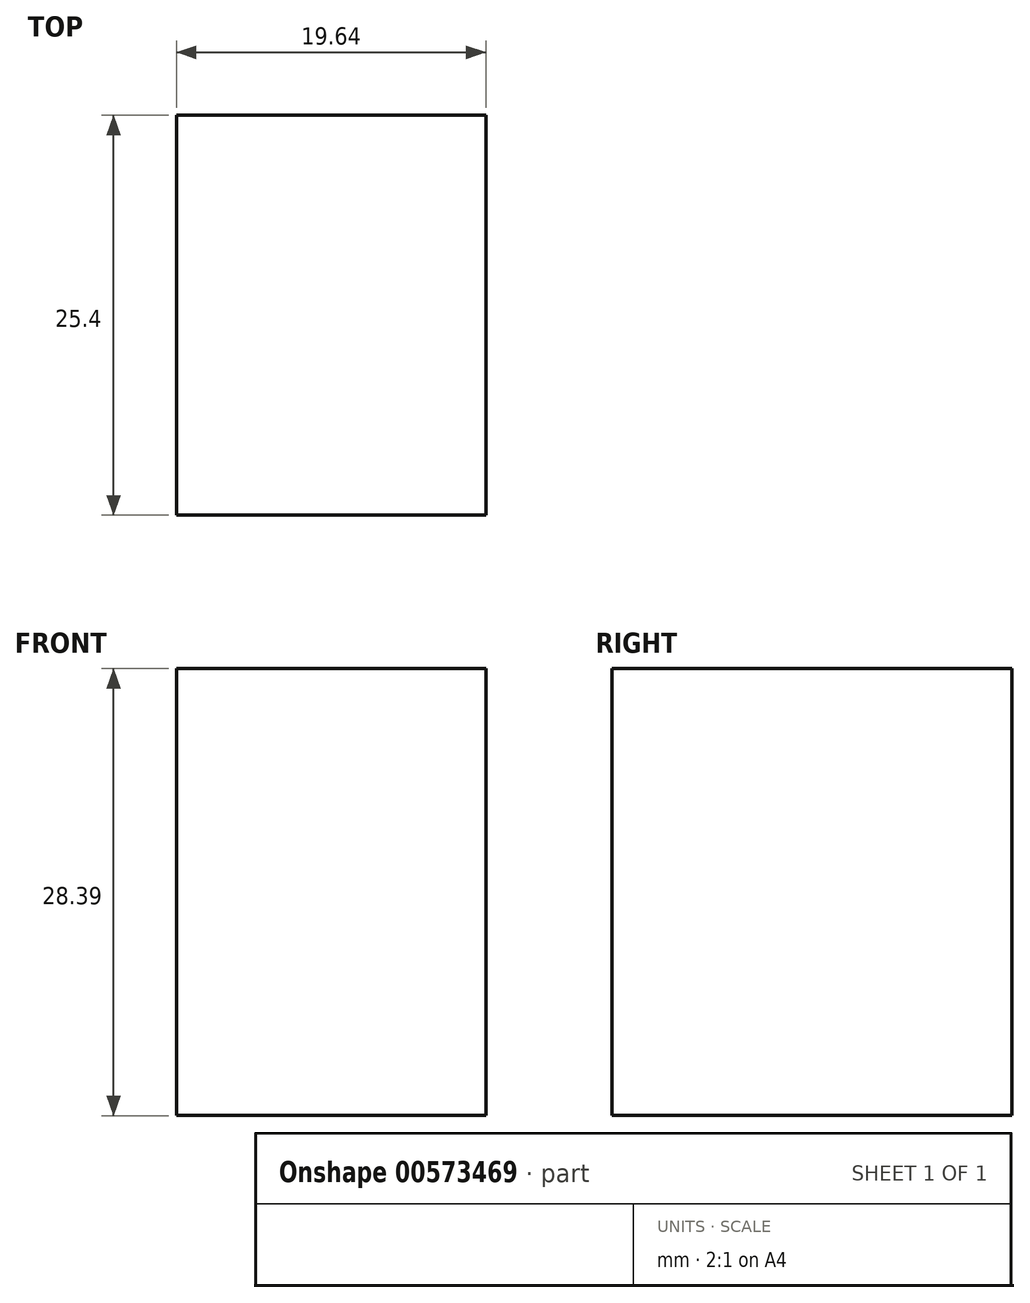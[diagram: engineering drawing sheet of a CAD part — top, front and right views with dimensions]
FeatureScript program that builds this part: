
annotation { "Feature Type Name" : "Feature", "Feature Type Description" : "" }
export const myFeature = defineFeature(function(context is Context, id is Id, definition is map)
    precondition{}
    {
        {
            var Q0;
            Q0=qCreatedBy(makeId("Front.planeOp"),FACE);
            var sketch = newSketch(context, id + "F0", { "sketchPlane" : qUnion([Q0])});
            skLineSegment(sketch, "E0.bottom", {"start": v(-20.6, 0) * mm, "end": v(-40.24, 0) * mm});
            skLineSegment(sketch, "E0.top", {"start": v(-20.6, -28.39) * mm, "end": v(-40.24, -28.39) * mm});
            skLineSegment(sketch, "E0.left", {"start": v(-20.6, 0) * mm, "end": v(-20.6, -28.39) * mm});
            skLineSegment(sketch, "E0.right", {"start": v(-40.24, 0) * mm, "end": v(-40.24, -28.39) * mm});
            skSolve(sketch);
        }
        {
            var Q0;
            Q0 = qSketchRegion(id + "F0", true);
            extrude(context, id + "F1", {"entities" : qUnion([Q0]), "depth" : 25.4 * mm, "offsetDistance" : 25.4 * mm});
        }
    });
